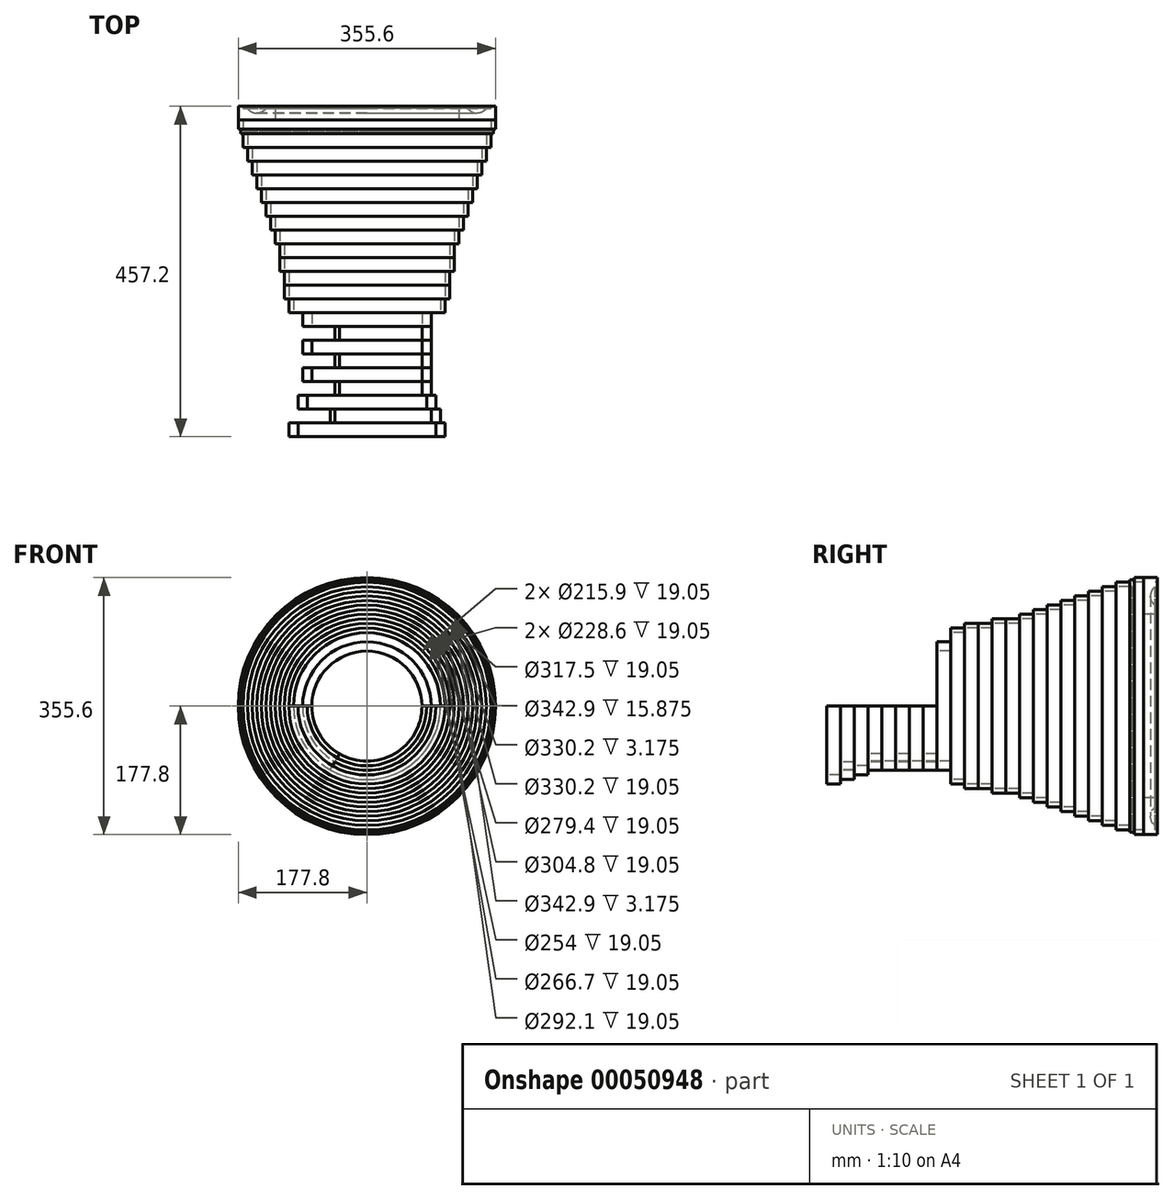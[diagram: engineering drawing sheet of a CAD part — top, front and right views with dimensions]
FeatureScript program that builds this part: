
annotation { "Feature Type Name" : "Feature", "Feature Type Description" : "" }
export const myFeature = defineFeature(function(context is Context, id is Id, definition is map)
    precondition{}
    {
        {
            var Q0;
            Q0=qCreatedBy(makeId("Top.planeOp"),FACE);
            var sketch = newSketch(context, id + "F0", { "sketchPlane" : qUnion([Q0])});
            skLineSegment(sketch, "E0", {"start": v(127, 15.87) * mm, "end": v(127, 0) * mm});
            skLineSegment(sketch, "E1", {"start": v(127, 0) * mm, "end": v(177.8, 0) * mm});
            skLineSegment(sketch, "E2", {"start": v(177.8, 0) * mm, "end": v(177.8, 19.05) * mm});
            skLineSegment(sketch, "E3", {"start": v(177.8, 19.05) * mm, "end": v(171.45, 19.05) * mm});
            skLineSegment(sketch, "E4", {"start": v(171.45, 19.05) * mm, "end": v(171.45, 15.88) * mm});
            skLineSegment(sketch, "E5", {"start": v(171.45, 15.88) * mm, "end": v(165.1, 15.88) * mm});
            skLineSegment(sketch, "E6.trimOffspring", {"start": v(139.7, 15.87) * mm, "end": v(127, 15.87) * mm});
            skArc(sketch, "E7", {"start": v(139.7, 15.87) * mm, "mid": v(152.4, 9.52) * mm, "end": v(165.1, 15.88) * mm});
            skLineSegment(sketch, "E8", {"start": v(0, 0) * mm, "end": v(0, 52.65) * mm, "construction": true});
            skSolve(sketch);
        }
        {
            var Q0;
            Q0=makeQuery(id+"F0.imprint","IMPRINT",FACE,{"disambiguationData":[TD([[makeQuery(id+"F0.imprint","IMPRINT",EDGE,{"derivedFrom":sQuery(id+"F0.wireOp",EDGE,"E0")}),1.0]])]});
            var Q1;
            Q1=sQuery(id+"F0.wireOp",EDGE,"E8");
            revolve(context, id + "F1", {"entities" : qUnion([Q0]), "axis" : qUnion([Q1]), "revolveType" : RevolveType.FULL});
        }
        {
            var Q0;
            Q0=qCreatedBy(makeId("Top.planeOp"),FACE);
            var sketch = newSketch(context, id + "F2", { "sketchPlane" : qUnion([Q0])});
            skLineSegment(sketch, "E9.bottom", {"start": v(177.8, 0) * mm, "end": v(171.45, 0) * mm});
            skLineSegment(sketch, "E9.left", {"start": v(177.8, 0) * mm, "end": v(177.8, -12.7) * mm});
            skLineSegment(sketch, "E9.right", {"start": v(171.45, 0) * mm, "end": v(171.45, -15.87) * mm});
            skLineSegment(sketch, "E10.bottom", {"start": v(171.45, -19.05) * mm, "end": v(165.1, -19.05) * mm});
            skLineSegment(sketch, "E10.top", {"start": v(171.45, -38.1) * mm, "end": v(165.1, -38.1) * mm});
            skLineSegment(sketch, "E10.left", {"start": v(171.45, -19.05) * mm, "end": v(171.45, -38.1) * mm});
            skLineSegment(sketch, "E10.right", {"start": v(165.1, -19.05) * mm, "end": v(165.1, -38.1) * mm});
            skLineSegment(sketch, "E11.bottom", {"start": v(165.1, -38.1) * mm, "end": v(158.75, -38.1) * mm});
            skLineSegment(sketch, "E11.top", {"start": v(165.1, -57.15) * mm, "end": v(158.75, -57.15) * mm});
            skLineSegment(sketch, "E11.left", {"start": v(165.1, -38.1) * mm, "end": v(165.1, -57.15) * mm});
            skLineSegment(sketch, "E11.right", {"start": v(158.75, -38.1) * mm, "end": v(158.75, -57.15) * mm});
            skLineSegment(sketch, "E12.bottom", {"start": v(158.75, -57.15) * mm, "end": v(152.4, -57.15) * mm});
            skLineSegment(sketch, "E12.top", {"start": v(158.75, -76.2) * mm, "end": v(152.4, -76.2) * mm});
            skLineSegment(sketch, "E12.left", {"start": v(158.75, -57.15) * mm, "end": v(158.75, -76.2) * mm});
            skLineSegment(sketch, "E12.right", {"start": v(152.4, -57.15) * mm, "end": v(152.4, -76.2) * mm});
            skLineSegment(sketch, "E13.right", {"start": v(133.35, -114.3) * mm, "end": v(133.35, -133.35) * mm});
            skLineSegment(sketch, "E13.left", {"start": v(139.7, -114.3) * mm, "end": v(139.7, -133.35) * mm});
            skLineSegment(sketch, "E14.right", {"start": v(139.7, -95.25) * mm, "end": v(139.7, -114.3) * mm});
            skLineSegment(sketch, "E14.left", {"start": v(146.05, -95.25) * mm, "end": v(146.05, -114.3) * mm});
            skLineSegment(sketch, "E15.right", {"start": v(127, -133.35) * mm, "end": v(127, -152.4) * mm});
            skLineSegment(sketch, "E16.right", {"start": v(146.05, -76.2) * mm, "end": v(146.05, -95.25) * mm});
            skLineSegment(sketch, "E16.left", {"start": v(152.4, -76.2) * mm, "end": v(152.4, -95.25) * mm});
            skLineSegment(sketch, "E15.left", {"start": v(133.35, -133.35) * mm, "end": v(133.35, -152.4) * mm});
            skLineSegment(sketch, "E16.bottom", {"start": v(152.4, -76.2) * mm, "end": v(146.05, -76.2) * mm});
            skLineSegment(sketch, "E15.top", {"start": v(133.35, -152.4) * mm, "end": v(127, -152.4) * mm});
            skLineSegment(sketch, "E15.bottom", {"start": v(133.35, -133.35) * mm, "end": v(127, -133.35) * mm});
            skLineSegment(sketch, "E13.top", {"start": v(139.7, -133.35) * mm, "end": v(133.35, -133.35) * mm});
            skLineSegment(sketch, "E13.bottom", {"start": v(139.7, -114.3) * mm, "end": v(133.35, -114.3) * mm});
            skLineSegment(sketch, "E14.top", {"start": v(146.05, -114.3) * mm, "end": v(139.7, -114.3) * mm});
            skLineSegment(sketch, "E14.bottom", {"start": v(146.05, -95.25) * mm, "end": v(139.7, -95.25) * mm});
            skLineSegment(sketch, "E16.top", {"start": v(152.4, -95.25) * mm, "end": v(146.05, -95.25) * mm});
            skLineSegment(sketch, "E17.left", {"start": v(120.65, -171.45) * mm, "end": v(120.65, -190.5) * mm});
            skLineSegment(sketch, "E17.right", {"start": v(114.3, -171.45) * mm, "end": v(114.3, -190.5) * mm});
            skLineSegment(sketch, "E18.right", {"start": v(120.65, -152.4) * mm, "end": v(120.65, -171.45) * mm});
            skLineSegment(sketch, "E18.left", {"start": v(127, -152.4) * mm, "end": v(127, -171.45) * mm});
            skLineSegment(sketch, "E17.top", {"start": v(120.65, -190.5) * mm, "end": v(114.3, -190.5) * mm});
            skLineSegment(sketch, "E18.top", {"start": v(127, -171.45) * mm, "end": v(120.65, -171.45) * mm});
            skLineSegment(sketch, "E18.bottom", {"start": v(127, -152.4) * mm, "end": v(120.65, -152.4) * mm});
            skLineSegment(sketch, "E17.bottom", {"start": v(120.65, -171.45) * mm, "end": v(114.3, -171.45) * mm});
            skLineSegment(sketch, "E19.right", {"start": v(114.3, -190.5) * mm, "end": v(114.3, -209.55) * mm});
            skLineSegment(sketch, "E19.left", {"start": v(120.65, -190.5) * mm, "end": v(120.65, -209.55) * mm});
            skLineSegment(sketch, "E19.top", {"start": v(120.65, -209.55) * mm, "end": v(114.3, -209.55) * mm});
            skLineSegment(sketch, "E20.right", {"start": v(107.95, -209.55) * mm, "end": v(107.95, -228.6) * mm});
            skLineSegment(sketch, "E20.left", {"start": v(114.3, -209.55) * mm, "end": v(114.3, -228.6) * mm});
            skLineSegment(sketch, "E20.top", {"start": v(114.3, -228.6) * mm, "end": v(107.95, -228.6) * mm});
            skLineSegment(sketch, "E20.bottom", {"start": v(114.3, -209.55) * mm, "end": v(107.95, -209.55) * mm});
            skLineSegment(sketch, "E21.right", {"start": v(107.95, -228.6) * mm, "end": v(107.95, -247.65) * mm});
            skLineSegment(sketch, "E21.left", {"start": v(114.3, -228.6) * mm, "end": v(114.3, -247.65) * mm});
            skLineSegment(sketch, "E21.top", {"start": v(114.3, -247.65) * mm, "end": v(107.95, -247.65) * mm});
            skLineSegment(sketch, "E22.right", {"start": v(101.6, -247.65) * mm, "end": v(101.6, -266.7) * mm});
            skLineSegment(sketch, "E22.left", {"start": v(107.95, -247.65) * mm, "end": v(107.95, -266.7) * mm});
            skLineSegment(sketch, "E22.top", {"start": v(107.95, -266.7) * mm, "end": v(101.6, -266.7) * mm});
            skLineSegment(sketch, "E22.bottom", {"start": v(107.95, -247.65) * mm, "end": v(101.6, -247.65) * mm});
            skLineSegment(sketch, "E23.right", {"start": v(76.2, -266.7) * mm, "end": v(76.2, -285.75) * mm});
            skLineSegment(sketch, "E23.left", {"start": v(88.9, -266.7) * mm, "end": v(88.9, -285.75) * mm});
            skLineSegment(sketch, "E23.top", {"start": v(88.9, -285.75) * mm, "end": v(76.2, -285.75) * mm});
            skLineSegment(sketch, "E23.bottom", {"start": v(88.9, -266.7) * mm, "end": v(76.2, -266.7) * mm});
            skLineSegment(sketch, "E24.right", {"start": v(76.2, -285.75) * mm, "end": v(76.2, -304.8) * mm});
            skLineSegment(sketch, "E24.left", {"start": v(88.9, -285.75) * mm, "end": v(88.9, -304.8) * mm});
            skLineSegment(sketch, "E24.top", {"start": v(88.9, -304.8) * mm, "end": v(76.2, -304.8) * mm});
            skLineSegment(sketch, "E25.right", {"start": v(76.2, -304.8) * mm, "end": v(76.2, -323.85) * mm});
            skLineSegment(sketch, "E25.left", {"start": v(88.9, -304.8) * mm, "end": v(88.9, -323.85) * mm});
            skLineSegment(sketch, "E25.top", {"start": v(88.9, -323.85) * mm, "end": v(76.2, -323.85) * mm});
            skLineSegment(sketch, "E26.right", {"start": v(76.2, -323.85) * mm, "end": v(76.2, -342.9) * mm});
            skLineSegment(sketch, "E26.left", {"start": v(88.9, -323.85) * mm, "end": v(88.9, -342.9) * mm});
            skLineSegment(sketch, "E26.top", {"start": v(88.9, -342.9) * mm, "end": v(76.2, -342.9) * mm});
            skLineSegment(sketch, "E27.right", {"start": v(76.2, -342.9) * mm, "end": v(76.2, -361.95) * mm});
            skLineSegment(sketch, "E27.left", {"start": v(88.9, -342.9) * mm, "end": v(88.9, -361.95) * mm});
            skLineSegment(sketch, "E27.top", {"start": v(88.9, -361.95) * mm, "end": v(76.2, -361.95) * mm});
            skLineSegment(sketch, "E28.right", {"start": v(76.2, -361.95) * mm, "end": v(76.2, -381) * mm});
            skLineSegment(sketch, "E28.left", {"start": v(88.9, -361.95) * mm, "end": v(88.9, -381) * mm});
            skLineSegment(sketch, "E28.top", {"start": v(88.9, -381) * mm, "end": v(76.2, -381) * mm});
            skLineSegment(sketch, "E29.right", {"start": v(82.55, -381) * mm, "end": v(82.55, -400.05) * mm});
            skLineSegment(sketch, "E29.left", {"start": v(95.25, -381) * mm, "end": v(95.25, -400.05) * mm});
            skLineSegment(sketch, "E29.top", {"start": v(95.25, -400.05) * mm, "end": v(82.55, -400.05) * mm});
            skLineSegment(sketch, "E29.bottom", {"start": v(95.25, -381) * mm, "end": v(82.55, -381) * mm});
            skLineSegment(sketch, "E30.right", {"start": v(88.9, -400.05) * mm, "end": v(88.9, -419.1) * mm});
            skLineSegment(sketch, "E30.left", {"start": v(101.6, -400.05) * mm, "end": v(101.6, -419.1) * mm});
            skLineSegment(sketch, "E30.top", {"start": v(101.6, -419.1) * mm, "end": v(88.9, -419.1) * mm});
            skLineSegment(sketch, "E30.bottom", {"start": v(101.6, -400.05) * mm, "end": v(88.9, -400.05) * mm});
            skLineSegment(sketch, "E31.right", {"start": v(95.25, -419.1) * mm, "end": v(95.25, -438.15) * mm});
            skLineSegment(sketch, "E31.left", {"start": v(107.95, -419.1) * mm, "end": v(107.95, -438.15) * mm});
            skLineSegment(sketch, "E31.top", {"start": v(107.95, -438.15) * mm, "end": v(95.25, -438.15) * mm});
            skLineSegment(sketch, "E31.bottom", {"start": v(107.95, -419.1) * mm, "end": v(95.25, -419.1) * mm});
            skLineSegment(sketch, "E32", {"start": v(171.45, -15.87) * mm, "end": v(165.1, -15.87) * mm});
            skLineSegment(sketch, "E33", {"start": v(165.1, -15.87) * mm, "end": v(165.1, -19.05) * mm});
            skPoint(sketch, "E9.top.end.orphan", {"position": v(171.45, -31.75) * mm});
            skLineSegment(sketch, "E34", {"start": v(174.62, -19.05) * mm, "end": v(165.1, -19.05) * mm});
            skLineSegment(sketch, "E35", {"start": v(174.62, -19.05) * mm, "end": v(174.62, -12.7) * mm});
            skLineSegment(sketch, "E36", {"start": v(174.62, -12.7) * mm, "end": v(177.8, -12.7) * mm});
            skLineSegment(sketch, "E37.1.0.0", {"start": v(190.5, 0) * mm, "end": v(184.15, 0) * mm});
            skLineSegment(sketch, "E37.1.0.1", {"start": v(184.15, 0) * mm, "end": v(184.15, -15.87) * mm});
            skLineSegment(sketch, "E37.1.0.2", {"start": v(190.5, 0) * mm, "end": v(190.5, -12.7) * mm});
            skLineSegment(sketch, "E37.1.0.3", {"start": v(187.32, -12.7) * mm, "end": v(190.5, -12.7) * mm});
            skLineSegment(sketch, "E37.1.0.4", {"start": v(187.32, -19.05) * mm, "end": v(187.32, -12.7) * mm});
            skLineSegment(sketch, "E37.1.0.5", {"start": v(184.15, -15.87) * mm, "end": v(177.8, -15.87) * mm});
            skLineSegment(sketch, "E37.1.0.6", {"start": v(177.8, -15.87) * mm, "end": v(177.8, -19.05) * mm});
            skLineSegment(sketch, "E37.1.0.7", {"start": v(187.32, -19.05) * mm, "end": v(177.8, -19.05) * mm});
            skLineSegment(sketch, "E37.direction1", {"start": v(171.45, 0) * mm, "end": v(184.15, 0) * mm, "construction": true});
            skSolve(sketch);
        }
        {
            var Q0;
            Q0=makeQuery(id+"F2.imprint","IMPRINT",FACE,{"disambiguationData":[TD([[makeQuery(id+"F2.imprint","IMPRINT",EDGE,{"derivedFrom":sQuery(id+"F2.wireOp",EDGE,"E9.bottom")}),1.0]])]});
            var Q1;
            {var subQ4=sQuery(id+"F2.wireOp",EDGE,"E12.top");Q1=makeQuery(id+"F2.imprint","IMPRINT",FACE,{"disambiguationData":[TD([[makeQuery(id+"F2.imprint","IMPRINT",EDGE,{"derivedFrom":subQ4}),-1.0]])]});}
            var Q2;
            {var subQ1=sQuery(id+"F2.wireOp",EDGE,"E13.right");Q2=makeQuery(id+"F2.imprint","IMPRINT",FACE,{"disambiguationData":[TD([[makeQuery(id+"F2.imprint","IMPRINT",EDGE,{"derivedFrom":subQ1}),1.0]])]});}
            var Q3;
            {var subQ1=sQuery(id+"F2.wireOp",EDGE,"E17.left");Q3=makeQuery(id+"F2.imprint","IMPRINT",FACE,{"disambiguationData":[TD([[makeQuery(id+"F2.imprint","IMPRINT",EDGE,{"derivedFrom":subQ1}),-1.0]])]});}
            var Q4;
            {var subQ3=sQuery(id+"F2.wireOp",EDGE,"E21.right");Q4=makeQuery(id+"F2.imprint","IMPRINT",FACE,{"disambiguationData":[TD([[makeQuery(id+"F2.imprint","IMPRINT",EDGE,{"derivedFrom":subQ3}),1.0]])]});}
            var Q5;
            Q5=sQuery(id+"F0.wireOp",EDGE,"E8");
            revolve(context, id + "F3", {"entities" : qUnion([Q0, Q1, Q2, Q3, Q4]), "axis" : qUnion([Q5]), "revolveType" : RevolveType.FULL});
        }
        {
            var Q0;
            {var subQ1=sQuery(id+"F2.wireOp",EDGE,"E10.top");Q0=makeQuery(id+"F2.imprint","IMPRINT",FACE,{"disambiguationData":[TD([[makeQuery(id+"F2.imprint","IMPRINT",EDGE,{"derivedFrom":subQ1}),-1.0]])]});}
            var Q1;
            {var subQ2=sQuery(id+"F2.wireOp",EDGE,"E16.right");Q1=makeQuery(id+"F2.imprint","IMPRINT",FACE,{"disambiguationData":[TD([[makeQuery(id+"F2.imprint","IMPRINT",EDGE,{"derivedFrom":subQ2}),1.0]])]});}
            var Q2;
            {var subQ2=sQuery(id+"F2.wireOp",EDGE,"E15.right");Q2=makeQuery(id+"F2.imprint","IMPRINT",FACE,{"disambiguationData":[TD([[makeQuery(id+"F2.imprint","IMPRINT",EDGE,{"derivedFrom":subQ2}),1.0]])]});}
            var Q3;
            {var subQ3=sQuery(id+"F2.wireOp",EDGE,"E19.right");Q3=makeQuery(id+"F2.imprint","IMPRINT",FACE,{"disambiguationData":[TD([[makeQuery(id+"F2.imprint","IMPRINT",EDGE,{"derivedFrom":subQ3}),1.0]])]});}
            var Q4;
            {var subQ4=sQuery(id+"F2.wireOp",EDGE,"E22.right");Q4=makeQuery(id+"F2.imprint","IMPRINT",FACE,{"disambiguationData":[TD([[makeQuery(id+"F2.imprint","IMPRINT",EDGE,{"derivedFrom":subQ4}),1.0]])]});}
            var Q5;
            Q5=sQuery(id+"F0.wireOp",EDGE,"E8");
            revolve(context, id + "F4", {"entities" : qUnion([Q0, Q1, Q2, Q3, Q4]), "axis" : qUnion([Q5]), "revolveType" : RevolveType.FULL});
        }
        {
            var Q0;
            {var subQ1=sQuery(id+"F2.wireOp",EDGE,"E11.top");Q0=makeQuery(id+"F2.imprint","IMPRINT",FACE,{"disambiguationData":[TD([[makeQuery(id+"F2.imprint","IMPRINT",EDGE,{"derivedFrom":subQ1}),-1.0]])]});}
            var Q1;
            {var subQ2=sQuery(id+"F2.wireOp",EDGE,"E14.right");Q1=makeQuery(id+"F2.imprint","IMPRINT",FACE,{"disambiguationData":[TD([[makeQuery(id+"F2.imprint","IMPRINT",EDGE,{"derivedFrom":subQ2}),1.0]])]});}
            var Q2;
            {var subQ3=sQuery(id+"F2.wireOp",EDGE,"E18.right");Q2=makeQuery(id+"F2.imprint","IMPRINT",FACE,{"disambiguationData":[TD([[makeQuery(id+"F2.imprint","IMPRINT",EDGE,{"derivedFrom":subQ3}),1.0]])]});}
            var Q3;
            {var subQ3=sQuery(id+"F2.wireOp",EDGE,"E20.right");Q3=makeQuery(id+"F2.imprint","IMPRINT",FACE,{"disambiguationData":[TD([[makeQuery(id+"F2.imprint","IMPRINT",EDGE,{"derivedFrom":subQ3}),1.0]])]});}
            var Q4;
            {var subQ2=sQuery(id+"F2.wireOp",EDGE,"E23.right");Q4=makeQuery(id+"F2.imprint","IMPRINT",FACE,{"disambiguationData":[TD([[makeQuery(id+"F2.imprint","IMPRINT",EDGE,{"derivedFrom":subQ2}),1.0]])]});}
            var Q5;
            Q5=sQuery(id+"F0.wireOp",EDGE,"E8");
            revolve(context, id + "F5", {"entities" : qUnion([Q0, Q1, Q2, Q3, Q4]), "axis" : qUnion([Q5]), "revolveType" : RevolveType.FULL});
        }
        {
            var Q0;
            Q0=makeQuery(id+"F2.imprint","IMPRINT",FACE,{"disambiguationData":[TD([[makeQuery(id+"F2.imprint","IMPRINT",EDGE,{"derivedFrom":sQuery(id+"F2.wireOp",EDGE,"E24.right")}),1.0]])]});
            var Q1;
            Q1=makeQuery(id+"F2.imprint","IMPRINT",FACE,{"disambiguationData":[TD([[makeQuery(id+"F2.imprint","IMPRINT",EDGE,{"derivedFrom":sQuery(id+"F2.wireOp",EDGE,"E26.right")}),1.0]])]});
            var Q2;
            Q2=makeQuery(id+"F2.imprint","IMPRINT",FACE,{"disambiguationData":[TD([[makeQuery(id+"F2.imprint","IMPRINT",EDGE,{"derivedFrom":sQuery(id+"F2.wireOp",EDGE,"E28.right")}),1.0]])]});
            var Q3;
            {var subQ4=sQuery(id+"F2.wireOp",EDGE,"E30.right");Q3=makeQuery(id+"F2.imprint","IMPRINT",FACE,{"disambiguationData":[TD([[makeQuery(id+"F2.imprint","IMPRINT",EDGE,{"derivedFrom":subQ4}),1.0]])]});}
            var Q4;
            Q4=sQuery(id+"F0.wireOp",EDGE,"E8");
            revolve(context, id + "F6", {"entities" : qUnion([Q0, Q1, Q2, Q3]), "axis" : qUnion([Q4]), "revolveType" : RevolveType.ONE_DIRECTION, "angle" : 120 * degree});
        }
        {
            var Q0;
            Q0=makeQuery(id+"F2.imprint","IMPRINT",FACE,{"disambiguationData":[TD([[makeQuery(id+"F2.imprint","IMPRINT",EDGE,{"derivedFrom":sQuery(id+"F2.wireOp",EDGE,"E25.right")}),1.0]])]});
            var Q1;
            Q1=makeQuery(id+"F2.imprint","IMPRINT",FACE,{"disambiguationData":[TD([[makeQuery(id+"F2.imprint","IMPRINT",EDGE,{"derivedFrom":sQuery(id+"F2.wireOp",EDGE,"E27.right")}),1.0]])]});
            var Q2;
            {var subQ3=sQuery(id+"F2.wireOp",EDGE,"E29.right");Q2=makeQuery(id+"F2.imprint","IMPRINT",FACE,{"disambiguationData":[TD([[makeQuery(id+"F2.imprint","IMPRINT",EDGE,{"derivedFrom":subQ3}),1.0]])]});}
            var Q3;
            {var subQ3=sQuery(id+"F2.wireOp",EDGE,"E31.right");Q3=makeQuery(id+"F2.imprint","IMPRINT",FACE,{"disambiguationData":[TD([[makeQuery(id+"F2.imprint","IMPRINT",EDGE,{"derivedFrom":subQ3}),1.0]])]});}
            var Q4;
            Q4=sQuery(id+"F0.wireOp",EDGE,"E8");
            revolve(context, id + "F7", {"entities" : qUnion([Q0, Q1, Q2, Q3]), "axis" : qUnion([Q4]), "revolveType" : RevolveType.ONE_DIRECTION, "angle" : 180 * degree});
        }
    });
